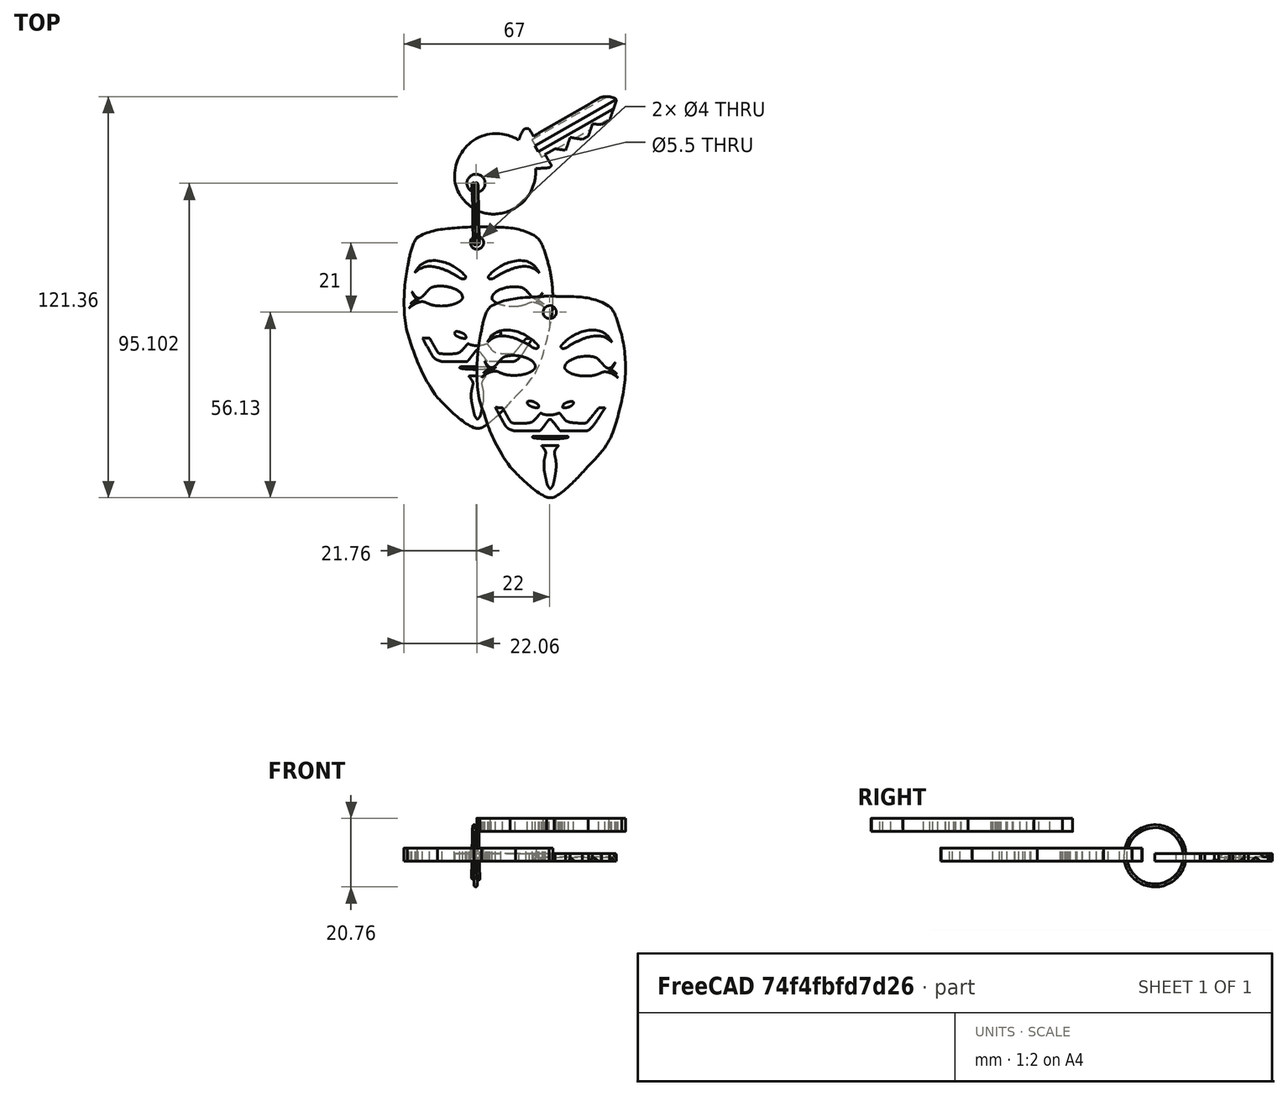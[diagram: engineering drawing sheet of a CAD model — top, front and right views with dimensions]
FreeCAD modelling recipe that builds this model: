
FCSTD DOCUMENT  (FreeCAD 0.14R3700 (Git))
Label: Vendetta
License: CC-BY 3.0
LicenseURL: http://creativecommons.org/licenses/by/3.0/
objects: Part::Feature×13, Part::Extrusion×10, Part::Cut×2, App::DocumentObjectGroup×2, Part::MultiFuse×1, Part::Cylinder×1
note: 27 computed .brp shape members not serialized (recipe doc carries the construction recipe); baked Part::Feature solids carry a one-line shape summary decoded from their .brp

FEATURE [Part::Feature] path3393  label="cara"
  shape: bbox 45.04 x 60.96 x 2e-07 mm, 1 faces, 0 solids (baked)
FEATURE [Part::Feature] path3389  label="perilla"
  shape: bbox 5.127 x 13.14 x 2e-07 mm, 1 faces, 0 solids (baked)
FEATURE [Part::Feature] path3385  label="boca"
  shape: bbox 10.9 x 0.8221 x 2e-07 mm, 1 faces, 0 solids (baked)
FEATURE [Part::Feature] path3383  label="bigote"
  shape: bbox 33.23 x 7.221 x 2e-07 mm, 1 faces, 0 solids (baked)
FEATURE [Part::Feature] path3381  label="nariz-i"
  shape: bbox 3.329 x 1.987 x 2e-07 mm, 1 faces, 0 solids (baked)
FEATURE [Part::Feature] path3379  label="nariz-d"
  shape: bbox 3.549 x 2.117 x 2e-07 mm, 1 faces, 0 solids (baked)
FEATURE [Part::Feature] path3377  label="ojo-i"
  shape: bbox 16.07 x 6.566 x 2e-07 mm, 1 faces, 0 solids (baked)
FEATURE [Part::Feature] path3373  label="ojo-d"
  shape: bbox 16.19 x 6.652 x 2e-07 mm, 1 faces, 0 solids (baked)
FEATURE [Part::Feature] path3367  label="ceja-i"
  shape: bbox 15.34 x 5.658 x 2e-07 mm, 1 faces, 0 solids (baked)
FEATURE [Part::Feature] path  label="ceja-d"
  Placement = pos=(44,0,0) rot=(0,1,0;3.14159rad)
  shape: bbox 15.34 x 5.658 x 2e-07 mm, 1 faces, 0 solids (baked)
FEATURE [Part::Extrusion] Extrude  label="ext-perilla"
  Base = -> path3389
  Dir = (0,0,20)
  Solid = true
FEATURE [Part::Extrusion] Extrude001  label="ext-boca"
  Base = -> path3385
  Dir = (0,0,20)
  Solid = true
FEATURE [Part::Extrusion] Extrude002  label="ext-bigote"
  Base = -> path3383
  Dir = (0,0,20)
  Solid = true
FEATURE [Part::Extrusion] Extrude003  label="ext-nariz-i"
  Base = -> path3381
  Dir = (0,0,20)
  Solid = true
FEATURE [Part::Extrusion] Extrude004  label="ext-nariz-d"
  Base = -> path3379
  Dir = (0,0,20)
  Solid = true
FEATURE [Part::Extrusion] Extrude005  label="ext-ojo-i"
  Base = -> path3377
  Dir = (0,0,20)
  Solid = true
FEATURE [Part::Extrusion] Extrude006  label="ext-ojo-d"
  Base = -> path3373
  Dir = (0,0,20)
  Solid = true
FEATURE [Part::Extrusion] Extrude007  label="ext-ceja-i"
  Base = -> path3367
  Dir = (0,0,20)
  Solid = true
FEATURE [Part::Extrusion] Extrude008  label="ext-ceja-d"
  Base = -> path
  Dir = (0,0,20)
  Solid = true
FEATURE [Part::Extrusion] Extrude009  label="ext-cara"
  Base = -> path3393
  Dir = (0,0,-4)
  Placement = pos=(0,0,13) rot=(0,0,1;0rad)
  Solid = true
FEATURE [Part::MultiFuse] Fusion  label="union-Rasgos"
  Shapes = -> [Extrude008,Extrude001,Extrude002,Extrude003,Extrude,Extrude005,Extrude006,Extrude004,Extrude007]
FEATURE [Part::Cut] Cut  label="Cara-completa"
  Base = -> Extrude009
  Tool = -> Fusion
FEATURE [Part::Cylinder] Cylinder  label="Agujero"
  Angle = 360
  Height = 10
  Placement = pos=(22,-5,6) rot=(0,0,1;0rad)
  Radius = 2
FEATURE [Part::Cut] Cut001  label="LlaVero"
  Base = -> Cut
  Tool = -> Cylinder
FEATURE [App::DocumentObjectGroup] Grupo  label="src"
  Group = -> [Cut001]
FEATURE [Part::Feature] Cut002  label="key-model"
  Placement = pos=(-5.46976,31.0266,0) rot=(0,0,1;0.517888rad)
  shape: bbox 49.82 x 36.6 x 2.3 mm, 44 faces (baked)
FEATURE [Part::Feature] Sweep  label="key-ring-model"
  Placement = pos=(-1.2,24.7546,1.6391) rot=(0.333333,0.881918,0.333333;1.69612rad)
  shape: bbox 3.31 x 27.02 x 26.33 mm, 4 faces (baked)
FEATURE [Part::Feature] Part__Feature  label="LlaVero-1"
  Placement = pos=(-22,21,-9) rot=(0,0,1;0rad)
  shape: bbox 45.04 x 60.96 x 4 mm, 152 faces (baked)
FEATURE [App::DocumentObjectGroup] Grupo001  label="Assembly"
  Group = -> [Cut002,Sweep,Part__Feature]
